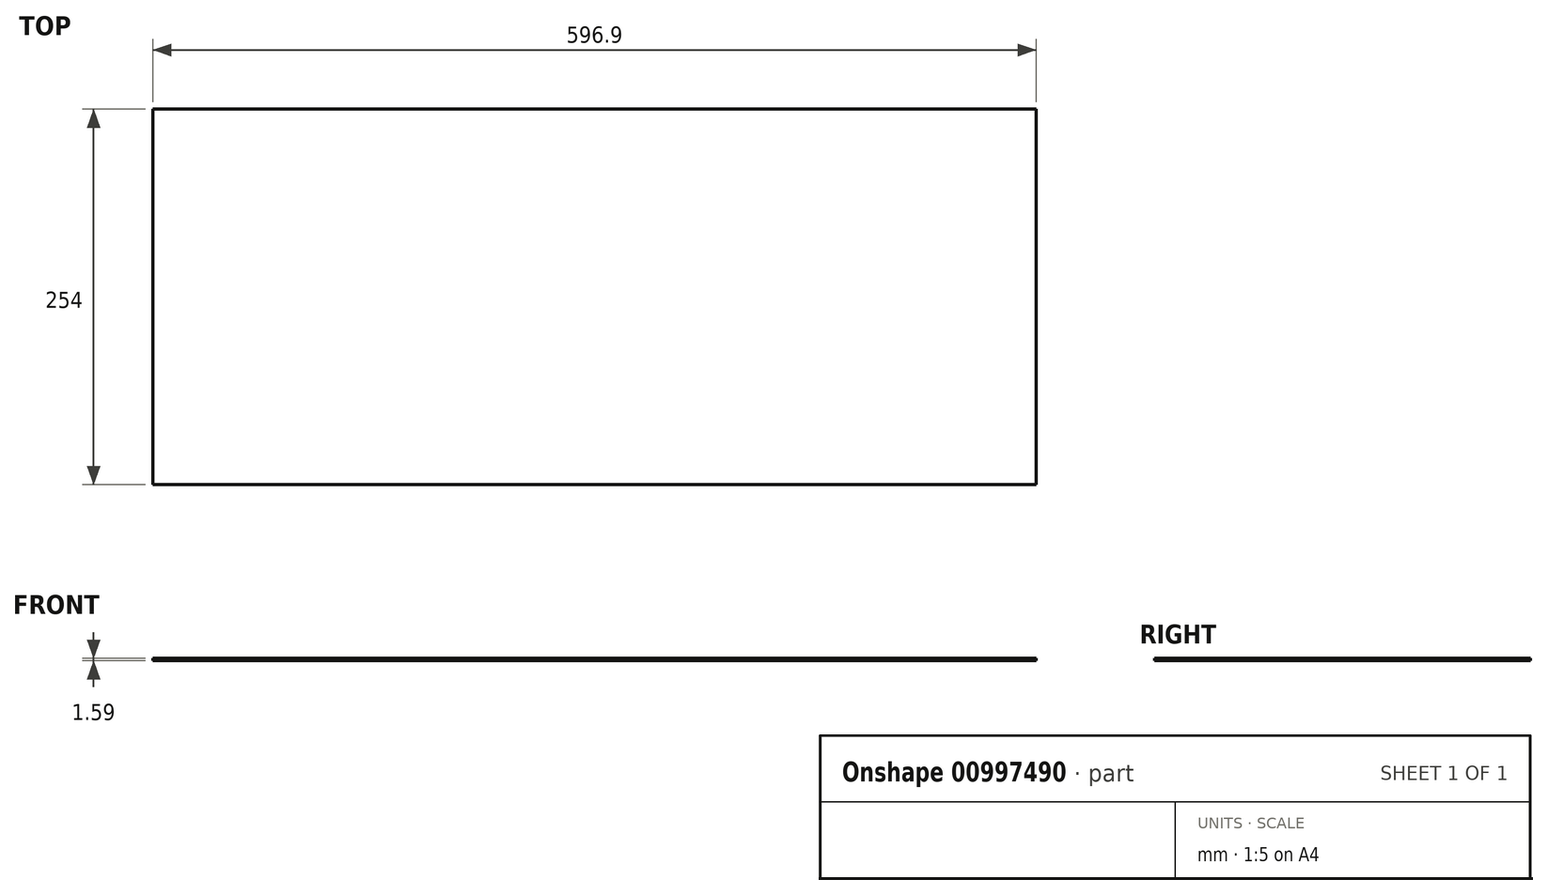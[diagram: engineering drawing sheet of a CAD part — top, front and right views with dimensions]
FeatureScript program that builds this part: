
annotation { "Feature Type Name" : "Feature", "Feature Type Description" : "" }
export const myFeature = defineFeature(function(context is Context, id is Id, definition is map)
    precondition{}
    {
        {
            var Q0;
            Q0=qCreatedBy(makeId("Top.planeOp"),FACE);
            var sketch = newSketch(context, id + "F0", { "sketchPlane" : qUnion([Q0])});
            skLineSegment(sketch, "E0.bottom", {"start": v(0, 0) * mm, "end": v(596.9, 0) * mm});
            skLineSegment(sketch, "E0.top", {"start": v(0, 254) * mm, "end": v(596.9, 254) * mm});
            skLineSegment(sketch, "E0.left", {"start": v(0, 0) * mm, "end": v(0, 254) * mm});
            skLineSegment(sketch, "E0.right", {"start": v(596.9, 0) * mm, "end": v(596.9, 254) * mm});
            skSolve(sketch);
        }
        {
            var Q0;
            Q0 = qSketchRegion(id + "F0", true);
            extrude(context, id + "F1", {"entities" : qUnion([Q0]), "depth" : 1.59 * mm, "offsetDistance" : 25.4 * mm});
        }
    });
